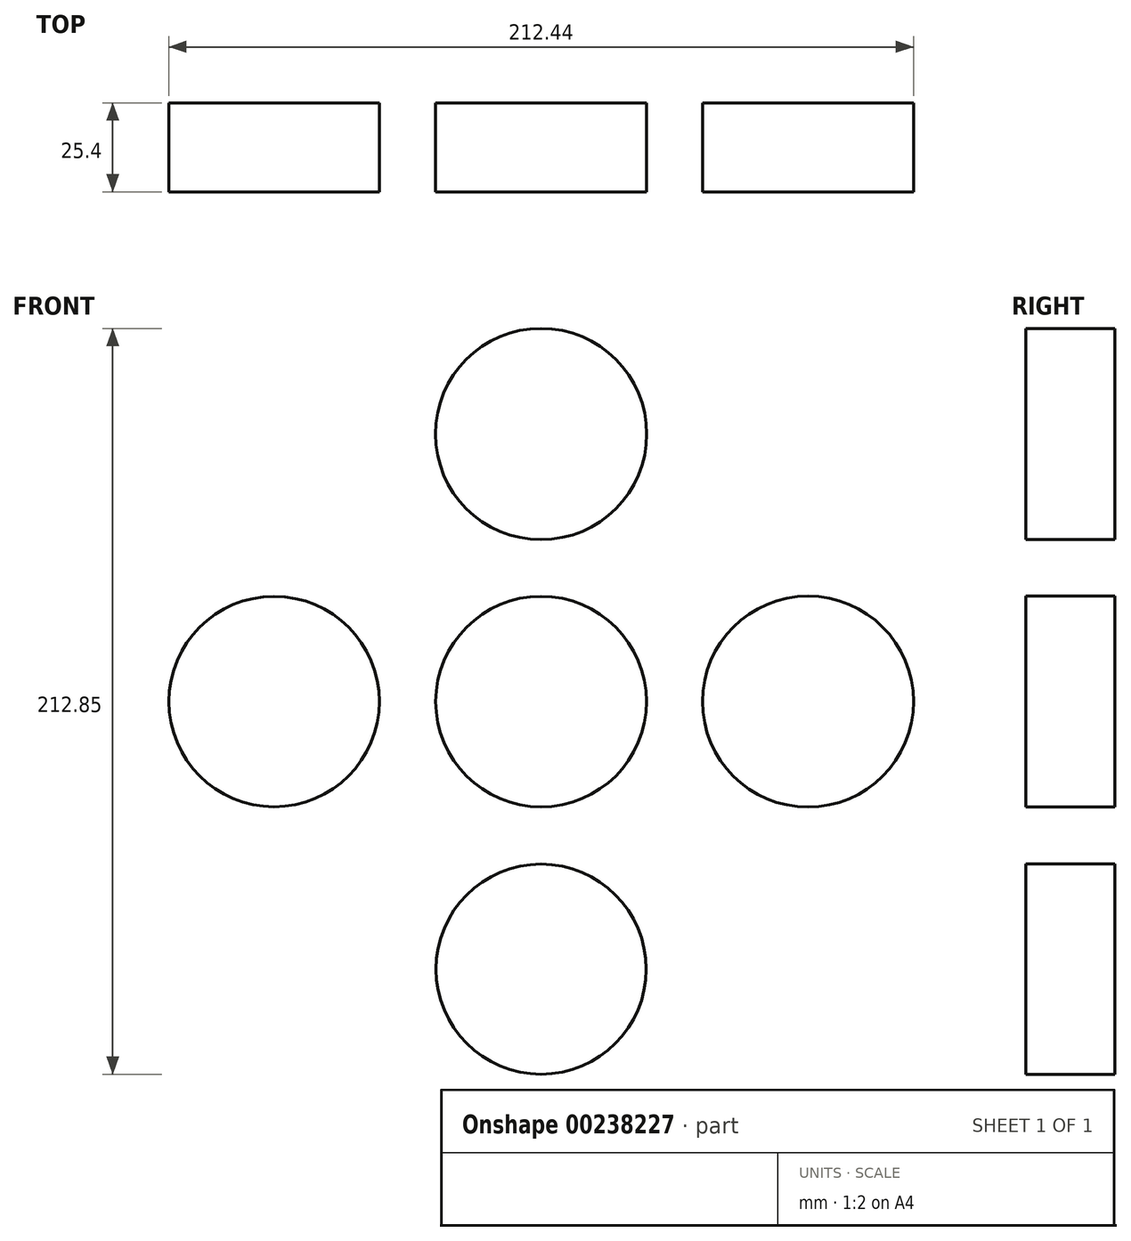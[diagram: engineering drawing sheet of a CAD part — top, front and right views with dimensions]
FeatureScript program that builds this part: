
annotation { "Feature Type Name" : "Feature", "Feature Type Description" : "" }
export const myFeature = defineFeature(function(context is Context, id is Id, definition is map)
    precondition{}
    {
        {
            var Q0;
            Q0=qCreatedBy(makeId("Front.planeOp"),FACE);
            var sketch = newSketch(context, id + "F0", { "sketchPlane" : qUnion([Q0])});
            skCircle(sketch, "E0", {"center": v(0, 0) * mm, "radius": 30.06 * mm});
            skCircle(sketch, "E1", {"center": v(76.16, 0) * mm, "radius": 30.1 * mm});
            skCircle(sketch, "E2", {"center": v(-76.16, 0) * mm, "radius": 30.02 * mm});
            skCircle(sketch, "E3", {"center": v(0, 76.36) * mm, "radius": 30.14 * mm});
            skCircle(sketch, "E4", {"center": v(0, -76.36) * mm, "radius": 29.98 * mm});
            skSolve(sketch);
        }
        {
            var Q0;
            Q0=makeQuery(id+"F0.imprint","IMPRINT",FACE,{"disambiguationData":[TD([[makeQuery(id+"F0.imprint","IMPRINT",EDGE,{"derivedFrom":sQuery(id+"F0.wireOp",EDGE,"E2")}),1.0]])]});
            var Q1;
            Q1=makeQuery(id+"F0.imprint","IMPRINT",FACE,{"disambiguationData":[TD([[makeQuery(id+"F0.imprint","IMPRINT",EDGE,{"derivedFrom":sQuery(id+"F0.wireOp",EDGE,"E0")}),1.0]])]});
            var Q2;
            Q2=makeQuery(id+"F0.imprint","IMPRINT",FACE,{"disambiguationData":[TD([[makeQuery(id+"F0.imprint","IMPRINT",EDGE,{"derivedFrom":sQuery(id+"F0.wireOp",EDGE,"E3")}),1.0]])]});
            var Q3;
            Q3=makeQuery(id+"F0.imprint","IMPRINT",FACE,{"disambiguationData":[TD([[makeQuery(id+"F0.imprint","IMPRINT",EDGE,{"derivedFrom":sQuery(id+"F0.wireOp",EDGE,"E1")}),1.0]])]});
            var Q4;
            Q4=makeQuery(id+"F0.imprint","IMPRINT",FACE,{"disambiguationData":[TD([[makeQuery(id+"F0.imprint","IMPRINT",EDGE,{"derivedFrom":sQuery(id+"F0.wireOp",EDGE,"E4")}),1.0]])]});
            extrude(context, id + "F1", {"entities" : qUnion([Q0, Q1, Q2, Q3, Q4]), "depth" : 25.4 * mm});
        }
    });
